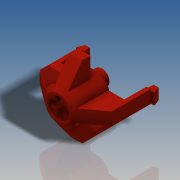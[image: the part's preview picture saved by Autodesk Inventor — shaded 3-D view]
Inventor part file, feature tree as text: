
AUTODESK INVENTOR PART (.ipt)
format: ipt  version: 2016 SP2 (Build 200236200, 236)  size: 466,432 bytes
history: native  units: in
note: dims shown in document units (in); Inventor stores cm internally (conversion verified against a paired STEP export)
features: sketch x5, extrude x5, revolve x2, mirror x1, fillet x1
ambient origin geometry x8: Origin, YZ Plane, XZ Plane, XY Plane, X Axis, Y Axis, Z Axis, Center Point
bodies: Solid1 (feature_tree)
feature tree (14):
  sketch  "Sketch2"  dims[d0=0.189in d1=0.315in]
  revolve  "Revolution1"  [1 undecoded]
  extrude  "Extrusion1"  Depth=0.315in
  extrude  "Extrusion2"  Depth=0.0315in
  mirror  "Mirror1"
  extrude  "Extrusion3"  Depth=0.3307in
  revolve  "Revolution2"  Angle=90.0deg
  extrude  "Extrusion4"  Depth=0.0039in
  extrude  "Extrusion5"  Depth=0.0039in
  fillet  "Fillet1"  Radius=0.063in
  sketch  "Sketch3"  dims[d2=0.0157in d3=0.315in]
  sketch  "Sketch4"  dims[d4=0.252in d5=0.0315in]
  sketch  "Sketch5"  dims[d6=0.2362in d7=0.3307in]
  sketch  "Sketch6"  dims[d8=0.1609in d9=90.0deg d10=0.0409in d11=0.0299in d12=0.063in d13=0.0472in d14=0.2047in d15=0.1206in d16=0.0in d17=0.0157in d18=0.0in d19=0.2362in d21=0.3307in d22=0.0409in d23=0.2362in d24=0.1206in d25=0.0in d26=0.0394in d27=90.0deg d28=0.1417in d29=0.0472in d30=0.0551in d31=0.0in d32=0.063in d33=0.2992in d34=0.0in d35=0.0039in]
note: 1 required parameter value undecoded (feature->parameter linkage not recoverable at this tier; creation-order binding heuristic only, values carry confidence <= 0.55)
